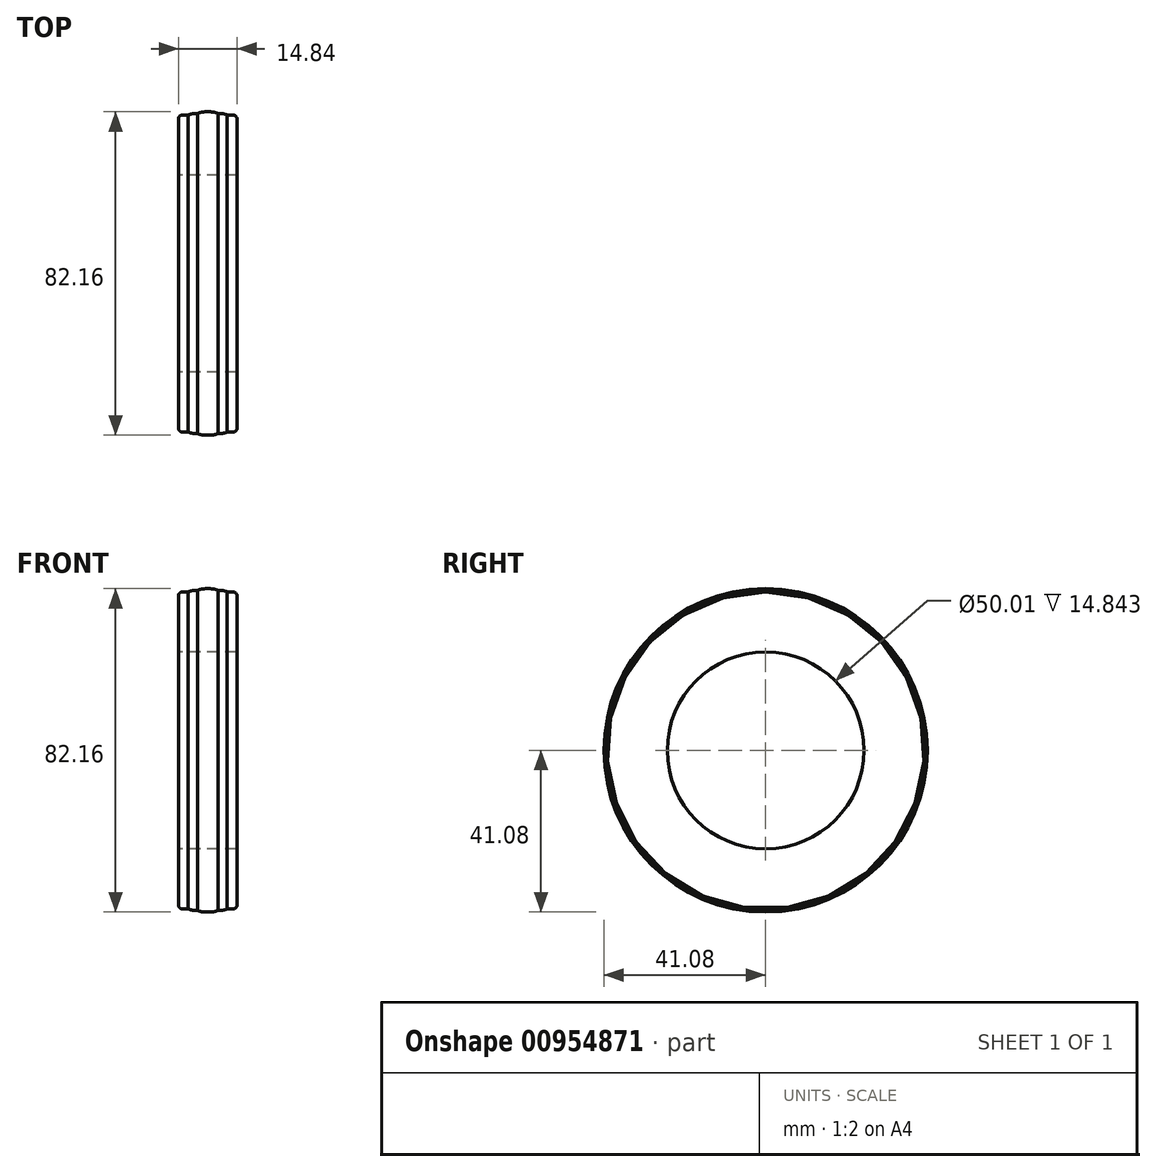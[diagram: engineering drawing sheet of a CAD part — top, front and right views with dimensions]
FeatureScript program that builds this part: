
annotation { "Feature Type Name" : "Feature", "Feature Type Description" : "" }
export const myFeature = defineFeature(function(context is Context, id is Id, definition is map)
    precondition{}
    {
        {
            var Q0;
            Q0=qCreatedBy(makeId("Front.planeOp"),FACE);
            var sketch = newSketch(context, id + "F0", { "sketchPlane" : qUnion([Q0])});
            skLineSegment(sketch, "E0", {"start": v(-55.67, 0) * mm, "end": v(68.03, 0) * mm, "construction": true});
            skLineSegment(sketch, "E1", {"start": v(-7.42, 0) * mm, "end": v(-7.42, 40.28) * mm});
            skLineSegment(sketch, "E2", {"start": v(-7.42, 40.28) * mm, "end": v(-4.96, 40.28) * mm});
            skLineSegment(sketch, "E3", {"start": v(-4.96, 40.28) * mm, "end": v(-4.96, 40.68) * mm});
            skLineSegment(sketch, "E4", {"start": v(-4.96, 40.68) * mm, "end": v(-2.58, 40.68) * mm});
            skLineSegment(sketch, "E5", {"start": v(-2.58, 40.68) * mm, "end": v(-2.58, 41.08) * mm});
            skLineSegment(sketch, "E6", {"start": v(-2.58, 41.08) * mm, "end": v(2.58, 41.08) * mm});
            skLineSegment(sketch, "E7", {"start": v(2.58, 41.08) * mm, "end": v(2.58, 40.68) * mm});
            skLineSegment(sketch, "E8", {"start": v(2.58, 40.68) * mm, "end": v(4.96, 40.68) * mm});
            skLineSegment(sketch, "E9", {"start": v(4.96, 40.68) * mm, "end": v(4.96, 40.28) * mm});
            skLineSegment(sketch, "E10", {"start": v(4.96, 40.28) * mm, "end": v(7.42, 40.28) * mm});
            skLineSegment(sketch, "E11", {"start": v(7.42, 40.28) * mm, "end": v(7.42, 0) * mm});
            skLineSegment(sketch, "E12", {"start": v(7.42, 0) * mm, "end": v(-7.42, 0) * mm});
            skLineSegment(sketch, "E13", {"start": v(0, 0) * mm, "end": v(0, 47.43) * mm, "construction": true});
            skSolve(sketch);
        }
        {
            var Q0;
            Q0=makeQuery(id+"F0.imprint","IMPRINT",FACE,{"disambiguationData":[TD([[makeQuery(id+"F0.imprint","IMPRINT",EDGE,{"derivedFrom":sQuery(id+"F0.wireOp",EDGE,"E1")}),-1.0]])]});
            var Q1;
            Q1=sQuery(id+"F0.wireOp",EDGE,"E0");
            revolve(context, id + "F1", {"surfaceOperationType" : NewSurfaceOperationType.NEW, "entities" : qUnion([Q0]), "axis" : qUnion([Q1]), "revolveType" : RevolveType.FULL});
        }
        {
            var Q0;
            Q0=makeQuery(id+"F1.opRevolve","SWEPT_EDGE",EDGE,{"disambiguationData":[OSD([sQuery(id+"F0.wireOp",EDGE,"E10"),sQuery(id+"F0.wireOp",EDGE,"E11")])]});
            var Q1;
            Q1=makeQuery(id+"F1.opRevolve","SWEPT_EDGE",EDGE,{"disambiguationData":[OSD([sQuery(id+"F0.wireOp",EDGE,"E1"),sQuery(id+"F0.wireOp",EDGE,"E2")])]});
            fillet(context, id + "F2", {"entities" : qUnion([Q0, Q1]), "radius" : 0.76 * mm, "tangentPropagation" : true, "rho" : 0.2, "crossSection" : FilletCrossSection.CONIC, "allowEdgeOverflow" : false});
        }
        {
            var Q0;
            Q0=makeQuery(id+"F1.opRevolve","SWEPT_EDGE",EDGE,{"disambiguationData":[OSD([sQuery(id+"F0.wireOp",EDGE,"E8"),sQuery(id+"F0.wireOp",EDGE,"E9")])]});
            var Q1;
            Q1=makeQuery(id+"F1.opRevolve","SWEPT_EDGE",EDGE,{"disambiguationData":[OSD([sQuery(id+"F0.wireOp",EDGE,"E3"),sQuery(id+"F0.wireOp",EDGE,"E4")])]});
            fillet(context, id + "F3", {"entities" : qUnion([Q0, Q1]), "radius" : 5.08 * mm, "tangentPropagation" : true, "allowEdgeOverflow" : false});
        }
        {
            var Q0;
            Q0=makeQuery(id+"F1.opRevolve","SWEPT_EDGE",EDGE,{"disambiguationData":[OSD([sQuery(id+"F0.wireOp",EDGE,"E6"),sQuery(id+"F0.wireOp",EDGE,"E7")])]});
            var Q1;
            Q1=makeQuery(id+"F1.opRevolve","SWEPT_EDGE",EDGE,{"disambiguationData":[OSD([sQuery(id+"F0.wireOp",EDGE,"E5"),sQuery(id+"F0.wireOp",EDGE,"E6")])]});
            fillet(context, id + "F4", {"entities" : qUnion([Q0, Q1]), "radius" : 5.08 * mm, "tangentPropagation" : true, "allowEdgeOverflow" : false});
        }
        {
            var Q0;
            Q0=qCreatedBy(makeId("Right.planeOp"),FACE);
            var sketch = newSketch(context, id + "F5", { "sketchPlane" : qUnion([Q0])});
            skCircle(sketch, "E14", {"center": v(0, 0) * mm, "radius": 25 * mm});
            skSolve(sketch);
        }
        {
            var Q0;
            Q0 = qSketchRegion(id + "F5", true);
            extrude(context, id + "F6", {"entities" : qUnion([Q0]), "operationType" : NewBodyOperationType.REMOVE, "endBound" : BoundingType.THROUGH_ALL, "depth" : 25.4 * mm, "offsetDistance" : 25.4 * mm, "hasSecondDirection" : true, "secondDirectionBound" : SecondDirectionBoundingType.THROUGH_ALL, "secondDirectionOppositeDirection" : true, "secondDirectionDepth" : 25.4 * mm});
        }
    });
